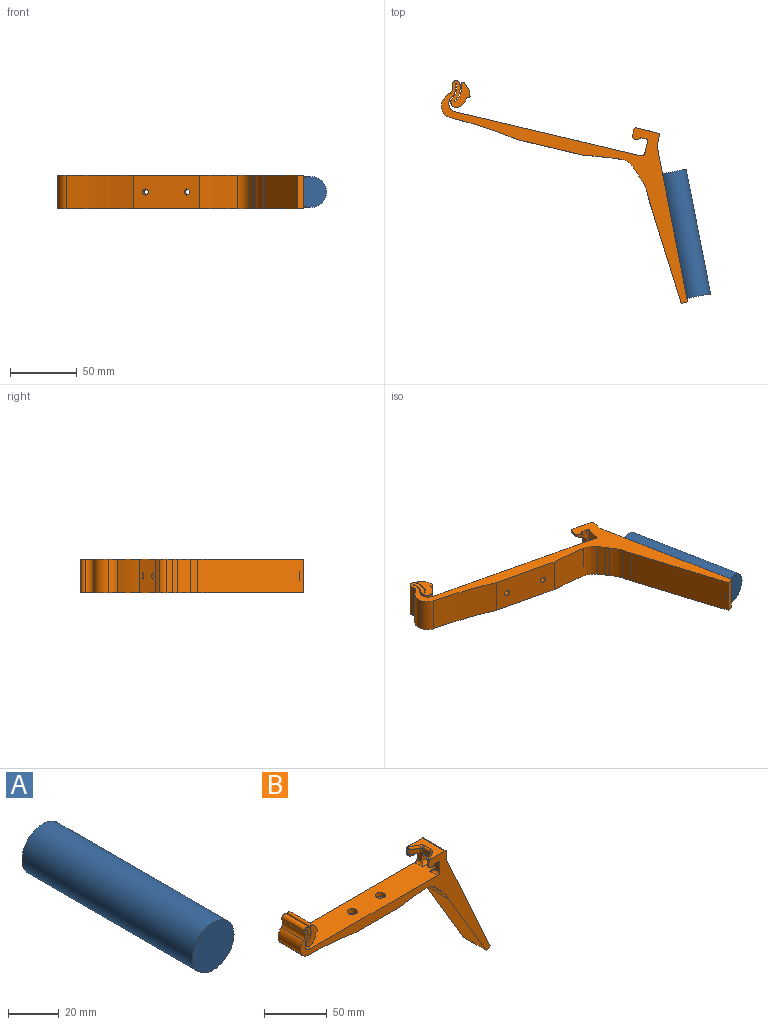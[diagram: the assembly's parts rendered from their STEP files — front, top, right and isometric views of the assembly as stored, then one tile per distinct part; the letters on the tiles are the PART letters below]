
ASSEMBLY  parts=2 mates=1
PART A: 3 faces, bbox 23.1x95.3x23.1 mm
  f0: cylinder r=11.56mm len=95.25mm, axis (0,1,0), area 6916.6mm2, adj f1,f2
  f1: plane 23.11x23.11mm, normal (0,-1,0), area 419.6mm2, adj f0
  f2: plane 23.11x23.11mm, normal (0,1,0), area 419.6mm2, adj f0
PART B: 94 faces, bbox 213.6x25.6x123.8 mm
  f0: plane 25.4x9.14mm, normal (-1,0,0), area 125.3mm2, adj f1,f30,f31,f40,f41,f71,f72,f73
  f1: cylinder r=2.54mm len=8.57mm, axis (0,1,0), area 26.7mm2, adj f0,f26,f31,f74
  f2: cylinder r=307.2mm len=28.56mm, axis (0,-1,0), area 731.3mm2, adj f30,f31,f50,f93
  f3: plane 4.57x0.87mm, normal (-1,0,0), area 4mm2, adj f4,f5,f31,f64,f67
  f4: cylinder r=1.52mm len=1.52mm, axis (0,1,0), area 1.7mm2, adj f3,f6,f31,f64
  f5: cylinder r=1.52mm len=1.5mm, axis (0,1,0), area 0.7mm2, adj f3,f31,f35,f67
  f6: plane 25.4x16.64mm, normal (0,0,1), area 236.2mm2, adj f4,f30,f31,f36,f37,f60,f61,f62
  f7: plane 25.4x10.36mm, normal (0,0,-1), area 66.2mm2, adj f9,f30,f31,f39,f40,f42,f43,f44
  f8: cylinder r=3.17mm len=5.66mm, axis (0,1,0), area 18.5mm2, adj f9,f30,f38,f42,f57
  f9: cylinder r=1.52mm len=4.16mm, axis (0,1,0), area 6.2mm2, adj f7,f8,f30,f42
  f10: cylinder r=10.92mm len=25.4mm, axis (0,1,0), area 282.7mm2, adj f11,f29,f30,f31
  f11: cylinder r=4.22mm len=25.4mm, axis (0,1,0), area 337mm2, adj f10,f12,f30,f31
  f12: plane 25.4x4.45mm, normal (0.85,0,-0.53), area 133.5mm2, adj f11,f13,f30,f31
  f13: plane 25.4x2.92mm, normal (1,0,0), area 74.2mm2, adj f12,f14,f30,f31
  f14: cylinder r=0.25mm len=25.4mm, axis (0,1,0), area 10.1mm2, adj f13,f15,f30,f31
  f15: plane 25.4x1.58mm, normal (0,0,-1), area 40.1mm2, adj f14,f30,f31,f32
  f16: plane 25.4x4.06mm, normal (0.94,0,0.34), area 109.7mm2, adj f17,f30,f31,f32
  f17: plane 25.4x4.49mm, normal (0.71,0,0.71), area 161.3mm2, adj f16,f18,f30,f31
  f18: cylinder r=1.59mm len=25.4mm, axis (0,1,0), area 126.7mm2, adj f17,f19,f30,f31
  f19: cylinder r=14.29mm len=25.4mm, axis (0,1,0), area 323.5mm2, adj f18,f20,f30,f31
  f20: cylinder r=0.41mm len=25.4mm, axis (0,1,0), area 32.9mm2, adj f19,f21,f30,f31
  f21: cylinder r=13.46mm len=25.4mm, axis (0,1,0), area 348.4mm2, adj f20,f22,f30,f31
  f22: cylinder r=2.95mm len=25.4mm, axis (0,1,0), area 242.9mm2, adj f21,f23,f30,f31
  f23: cylinder r=5.08mm len=25.4mm, axis (0,1,0), area 183.5mm2, adj f22,f24,f30,f31
  f24: cylinder r=10.16mm len=25.4mm, axis (0,1,0), area 333.7mm2, adj f23,f25,f30,f31
  f25: cylinder r=8.64mm len=25.4mm, axis (0,1,0), area 251.5mm2, adj f24,f30,f31,f49
  f26: plane 150.59x25.4mm, normal (0,0,1), area 3589.7mm2, adj f1,f27,f30,f31,f41,f53,f56,f74
  f27: cylinder r=6.35mm len=25.4mm, axis (0,1,0), area 339.5mm2, adj f26,f28,f30,f31
  f28: cylinder r=10.1mm len=25.4mm, axis (0,1,0), area 274.8mm2, adj f27,f29,f30,f31
  f29: cylinder r=0.41mm len=25.4mm, axis (0,1,0), area 32.9mm2, adj f10,f28,f30,f31
  f30: plane 213.37x123.55mm, normal (0,-1,0), area 2916.9mm2, adj f0,f2,f6,f7,f8,f9,f10,f11
  f31: plane 213.37x123.55mm, normal (0,1,0), area 2916.9mm2, adj f0,f1,f2,f3,f4,f5,f6,f7
  f32: cylinder r=0.76mm len=25.4mm, axis (0,-1,0), area 37.2mm2, adj f15,f16,f30,f31
  f33: plane 25.4x7.87mm, normal (1,0,0), area 184.1mm2, adj f30,f31,f36,f83,f84,f85,f86
  f34: plane 4.57x0.87mm, normal (-1,0,0), area 4mm2, adj f30,f37,f38,f57,f58
  f35: cylinder r=3.17mm len=5.66mm, axis (0,1,0), area 18.5mm2, adj f5,f31,f39,f43,f67
  f36: cylinder r=1.52mm len=25.4mm, axis (0,1,0), area 60.8mm2, adj f6,f30,f31,f33
  f37: cylinder r=1.52mm len=1.52mm, axis (0,1,0), area 1.7mm2, adj f6,f30,f34,f58
  f38: cylinder r=1.52mm len=1.5mm, axis (0,1,0), area 0.7mm2, adj f8,f30,f34,f57
  f39: cylinder r=1.52mm len=4.16mm, axis (0,1,0), area 6.2mm2, adj f7,f31,f35,f43
  f40: cylinder r=1.52mm len=25.4mm, axis (0,-1,0), area 60.8mm2, adj f0,f7,f30,f31
  f41: cylinder r=2.54mm len=8.57mm, axis (0,1,0), area 26.7mm2, adj f0,f26,f30,f77
  f42: plane 7.1x2.72mm, normal (-0.34,0.94,0), area 11mm2, adj f7,f8,f9,f57
  f43: plane 7.1x2.72mm, normal (-0.34,-0.94,0), area 11mm2, adj f7,f35,f39,f67
  f44: plane 7.19x4.57mm, normal (-1,0,0), area 32.9mm2, adj f7,f47,f48,f62
  f45: plane 7.96x4.57mm, normal (-0.49,0.87,0), area 41.8mm2, adj f7,f48,f57,f60
  f46: plane 7.96x4.57mm, normal (-0.49,-0.87,0), area 41.8mm2, adj f7,f47,f65,f67
  f47: cylinder r=2.54mm len=4.57mm, axis (0,0,-1), area 12.3mm2, adj f7,f44,f46,f63
  f48: cylinder r=2.54mm len=4.57mm, axis (0,0,1), area 12.3mm2, adj f7,f44,f45,f61
  f49: cylinder r=313.18mm len=52.58mm, axis (0,-1,0), area 1341.8mm2, adj f25,f30,f31,f50
  f50: plane 50.8x25.4mm, normal (0,0,-1), area 1258.6mm2, adj f2,f30,f31,f49,f51,f54
  f51: cylinder r=2.25mm len=5.36mm, axis (0,0,1), area 75.7mm2, adj f50,f52
  f52: plane 7.94x7.94mm, normal (0,0,1), area 33.6mm2, adj f51,f53
  f53: cylinder r=3.97mm len=7.94mm, axis (0,0,1), area 103.9mm2, adj f26,f52
  f54: cylinder r=2.25mm len=5.36mm, axis (0,0,1), area 75.7mm2, adj f50,f55
  f55: plane 7.94x7.94mm, normal (0,0,1), area 33.6mm2, adj f54,f56
  f56: cylinder r=3.97mm len=7.94mm, axis (0,0,1), area 103.9mm2, adj f26,f55
  f57: cylinder r=1.78mm len=5.28mm, axis (0,0,-1), area 8.9mm2, adj f7,f8,f34,f38,f42,f45,f59
  f58: bspline ~1.56x1.52mm, area 1.3mm2, adj f34,f37,f59,f60
  f59: bspline ~1.65x1.6mm, area 1.9mm2, adj f57,f58,f60
  f60: cylinder r=1.78mm len=9.08mm, axis (-0.87,-0.49,0), area 25.9mm2, adj f6,f45,f58,f59,f61
  f61: torus R=4.32mm, axis (0,0,-1), area 9.4mm2, adj f6,f48,f60,f62
  f62: cylinder r=1.78mm len=7.19mm, axis (0,-1,0), area 20.1mm2, adj f6,f44,f61,f63
  f63: torus R=4.32mm, axis (0,0,-1), area 9.4mm2, adj f6,f47,f62,f65
  f64: bspline ~1.67x1.66mm, area 1.3mm2, adj f3,f4,f65,f66
  f65: cylinder r=1.78mm len=9.08mm, axis (0.87,-0.49,0), area 25.9mm2, adj f6,f46,f63,f64,f66
  f66: bspline ~1.65x1.6mm, area 1.9mm2, adj f64,f65,f67
  f67: cylinder r=1.78mm len=5.28mm, axis (0,0,1), area 8.9mm2, adj f3,f5,f7,f35,f43,f46,f66
  f68: plane 25.4x4.26mm, normal (0.46,0,-0.89), area 121.5mm2, adj f30,f31,f86,f90
  f69: cylinder r=23.04mm len=25.4mm, axis (0,1,0), area 280.6mm2, adj f30,f31,f70,f91
  f70: plane 25.4x5.28mm, normal (-0.89,0,-0.46), area 150.8mm2, adj f30,f31,f69,f90
  f71: plane 8.26x5.42mm, normal (0,0,-1), area 44.7mm2, adj f0,f75,f76,f85
  f72: plane 5.42x3.81mm, normal (0,-1,0), area 20.7mm2, adj f0,f74,f75,f81
  f73: plane 5.42x3.81mm, normal (0,1,0), area 20.7mm2, adj f0,f76,f77,f82
  f74: cylinder r=3.17mm len=7.96mm, axis (1,0,0), area 31.1mm2, adj f0,f1,f26,f72,f79
  f75: cylinder r=3.17mm len=5.42mm, axis (1,0,0), area 27mm2, adj f0,f71,f72,f83
  f76: cylinder r=3.17mm len=5.42mm, axis (-1,0,0), area 27mm2, adj f0,f71,f73,f84
  f77: cylinder r=3.17mm len=7.96mm, axis (-1,0,0), area 31.1mm2, adj f0,f26,f41,f73,f80
  f78: plane 9.21x8.26mm, normal (0.5,0,0.87), area 87.8mm2, adj f26,f79,f80,f86
  f79: cone r=4.45mm half-angle=30deg, axis (1,0,0), area 75.5mm2, adj f74,f78,f81,f86
  f80: cone r=4.45mm half-angle=30deg, axis (1,0,0), area 75.5mm2, adj f77,f78,f82,f86
  f81: plane 5.36x3.81mm, normal (0.5,-0.87,0), area 19.8mm2, adj f72,f79,f83,f86
  f82: plane 5.36x3.81mm, normal (0.5,0.87,0), area 19.8mm2, adj f73,f80,f84,f86
  f83: cone r=4.45mm half-angle=30deg, axis (1,0,0), area 18mm2, adj f33,f75,f81,f85,f86
  f84: cone r=4.45mm half-angle=30deg, axis (1,0,0), area 18mm2, adj f33,f76,f82,f85,f86
  f85: plane 8.26x2.2mm, normal (0.5,0,-0.87), area 21mm2, adj f33,f71,f83,f84
  f86: plane 108.53x49.15mm, normal (0.91,0,0.41), area 876mm2, adj f30,f31,f33,f68,f78,f79,f80,f81
  f87: cylinder r=11.6mm len=88.98mm, axis (0.41,0,-0.91), area 2155.1mm2, adj f86,f88,f89
  f88: plane 19.19x4.63mm, normal (0.41,0,-0.91), area 68.5mm2, adj f86,f87
  f89: plane 19.19x4.63mm, normal (-0.41,0,0.91), area 68.5mm2, adj f86,f87
  f90: plane 71.14x42.19mm, normal (-0.86,0,-0.51), area 2100.7mm2, adj f30,f31,f68,f70
  f91: plane 25.4x2.94mm, normal (-0.71,0,-0.71), area 105.6mm2, adj f30,f31,f69,f92
  f92: plane 25.4x3.72mm, normal (-0.69,0,-0.73), area 129.9mm2, adj f30,f31,f91,f93
  f93: cylinder r=12.7mm len=25.4mm, axis (0,-1,0), area 268.7mm2, adj f2,f30,f31,f92
PLACE A rot(axis=(0,0,1),11deg) t=(75.19,-4.14,-57.05)mm
PLACE B rot(axis=(-0.99,0.12,-0.12),90.8deg) t=(-22.14,70.28,-57.05)mm
MATE fastened B.f87 <-> A.f0  axis (0.19,-0.98,0) through (84.31,-50.88,-57.05)mm
